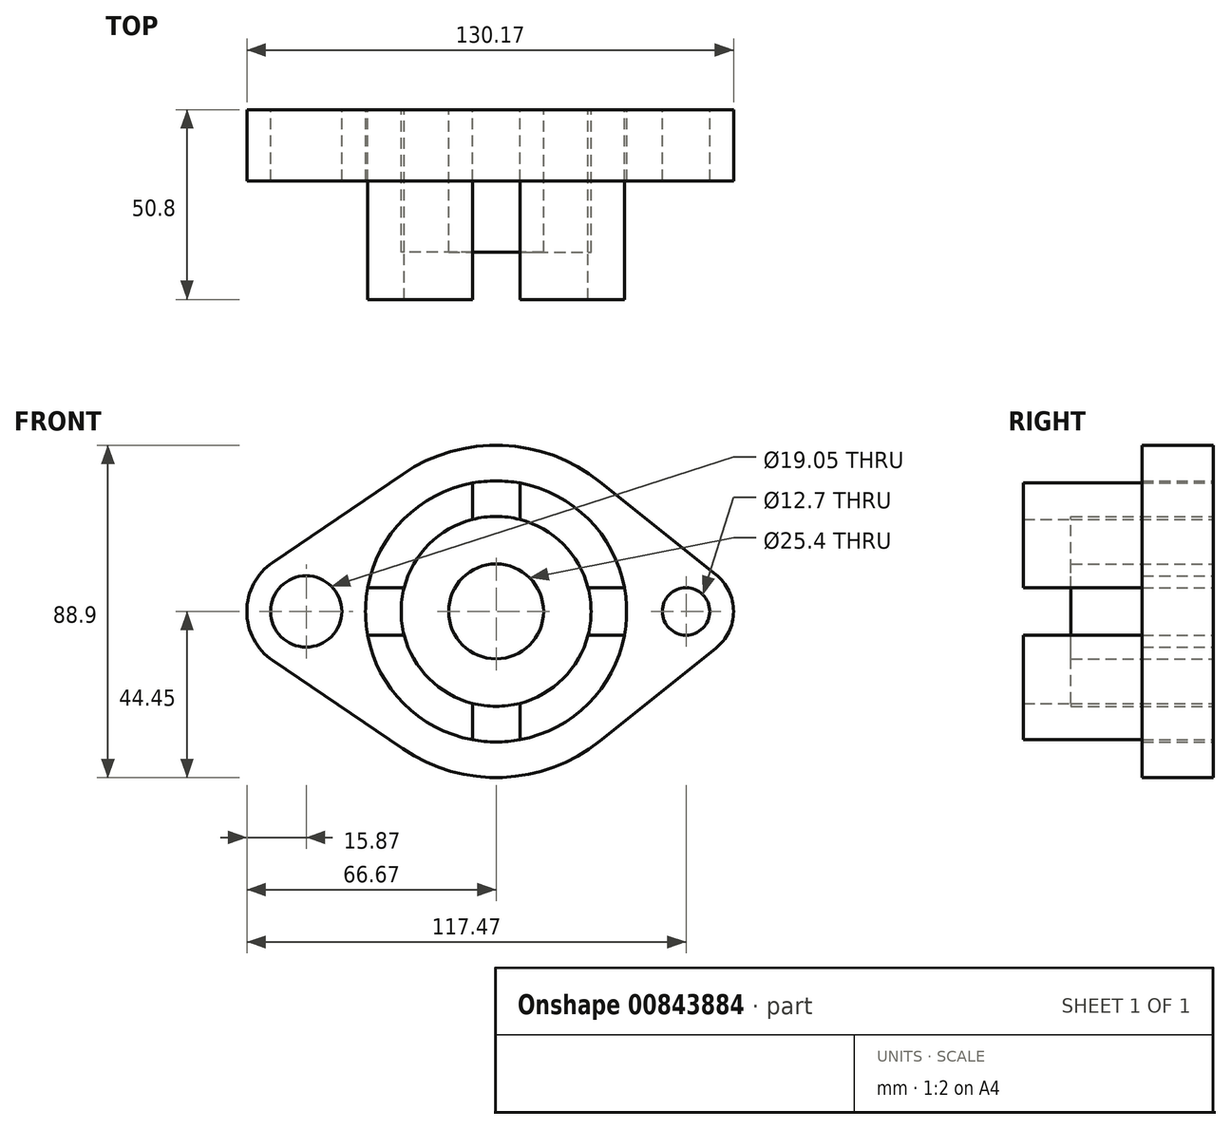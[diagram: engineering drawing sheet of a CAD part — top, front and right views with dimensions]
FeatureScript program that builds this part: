
annotation { "Feature Type Name" : "Feature", "Feature Type Description" : "" }
export const myFeature = defineFeature(function(context is Context, id is Id, definition is map)
    precondition{}
    {
        {
            var Q0;
            Q0=qCreatedBy(makeId("Front.planeOp"),FACE);
            var sketch = newSketch(context, id + "F0", { "sketchPlane" : qUnion([Q0])});
            skCircle(sketch, "E0", {"center": v(0, 0) * mm, "radius": 12.7 * mm});
            skCircle(sketch, "E1", {"center": v(0, 0) * mm, "radius": 25.4 * mm});
            skCircle(sketch, "E2", {"center": v(0, 0) * mm, "radius": 34.93 * mm});
            skLineSegment(sketch, "E3", {"start": v(24.6, 6.35) * mm, "end": v(34.34, 6.35) * mm});
            skLineSegment(sketch, "E4", {"start": v(24.6, -6.35) * mm, "end": v(34.34, -6.35) * mm});
            skLineSegment(sketch, "E5", {"start": v(6.35, 24.6) * mm, "end": v(6.35, 34.34) * mm});
            skLineSegment(sketch, "E6", {"start": v(-6.35, 24.6) * mm, "end": v(-6.35, 34.34) * mm});
            skLineSegment(sketch, "E7", {"start": v(-24.6, 6.35) * mm, "end": v(-34.34, 6.35) * mm});
            skLineSegment(sketch, "E8", {"start": v(-24.6, -6.35) * mm, "end": v(-34.34, -6.35) * mm});
            skLineSegment(sketch, "E9", {"start": v(6.35, -24.6) * mm, "end": v(6.35, -34.34) * mm});
            skLineSegment(sketch, "E10", {"start": v(-6.35, -24.6) * mm, "end": v(-6.35, -34.34) * mm});
            skLineSegment(sketch, "E11", {"start": v(0, 0) * mm, "end": v(50.8, 0) * mm});
            skLineSegment(sketch, "E12", {"start": v(0, 0) * mm, "end": v(-50.8, 0) * mm});
            skCircle(sketch, "E13", {"center": v(50.8, 0) * mm, "radius": 6.35 * mm});
            skCircle(sketch, "E14", {"center": v(-50.8, 0) * mm, "radius": 9.53 * mm});
            skArc(sketch, "E15", {"start": v(-25, -36.75) * mm, "mid": v(1.73, -44.42) * mm, "end": v(27.78, -34.7) * mm});
            skArc(sketch, "E16", {"start": v(58.74, -9.91) * mm, "mid": v(63.5, 0) * mm, "end": v(58.74, 9.91) * mm});
            skArc(sketch, "E17", {"start": v(-59.73, 13.13) * mm, "mid": v(-66.68, 0) * mm, "end": v(-59.73, -13.13) * mm});
            skLineSegment(sketch, "E18", {"start": v(58.74, 9.91) * mm, "end": v(27.78, 34.7) * mm});
            skLineSegment(sketch, "E19", {"start": v(27.78, -34.7) * mm, "end": v(58.74, -9.91) * mm});
            skLineSegment(sketch, "E20", {"start": v(-59.73, -13.13) * mm, "end": v(-25, -36.75) * mm});
            skLineSegment(sketch, "E21", {"start": v(-59.73, 13.13) * mm, "end": v(-25, 36.75) * mm});
            skArc(sketch, "E22.trimOffspring", {"start": v(27.78, 34.7) * mm, "mid": v(1.73, 44.42) * mm, "end": v(-25, 36.75) * mm});
            skSolve(sketch);
        }
        {
            var Q0;
            Q0=makeQuery(id+"F0.imprint","IMPRINT",FACE,{"disambiguationData":[TD([[makeQuery(id+"F0.imprint","IMPRINT",EDGE,{"derivedFrom":sQuery(id+"F0.wireOp",EDGE,"E13")}),-1.0]])]});
            extrude(context, id + "F1", {"entities" : qUnion([Q0]), "depth" : 19.05 * mm, "offsetDistance" : 25.4 * mm});
        }
        {
            var Q0;
            {var subQ0=sQuery(id+"F0.wireOp",EDGE,"E6");Q0=makeQuery(id+"F0.imprint","IMPRINT",FACE,{"disambiguationData":[TD([[makeQuery(id+"F0.imprint","IMPRINT",EDGE,{"derivedFrom":subQ0}),1.0]])]});}
            var Q1;
            {var subQ0=sQuery(id+"F0.wireOp",EDGE,"E3");Q1=makeQuery(id+"F0.imprint","IMPRINT",FACE,{"disambiguationData":[TD([[makeQuery(id+"F0.imprint","IMPRINT",EDGE,{"derivedFrom":subQ0}),1.0]])]});}
            var Q2;
            {var subQ0=sQuery(id+"F0.wireOp",EDGE,"E4");Q2=makeQuery(id+"F0.imprint","IMPRINT",FACE,{"disambiguationData":[TD([[makeQuery(id+"F0.imprint","IMPRINT",EDGE,{"derivedFrom":subQ0}),-1.0]])]});}
            var Q3;
            {var subQ0=sQuery(id+"F0.wireOp",EDGE,"E8");Q3=makeQuery(id+"F0.imprint","IMPRINT",FACE,{"disambiguationData":[TD([[makeQuery(id+"F0.imprint","IMPRINT",EDGE,{"derivedFrom":subQ0}),1.0]])]});}
            extrude(context, id + "F2", {"entities" : qUnion([Q0, Q1, Q2, Q3]), "operationType" : NewBodyOperationType.ADD, "depth" : 50.8 * mm, "offsetDistance" : 25.4 * mm});
        }
        {
            var Q0;
            {var subQ3=sQuery(id+"F0.wireOp",EDGE,"E11");var subQ4=sQuery(id+"F0.wireOp",EDGE,"E0");var subQ5=makeQuery(id+"F0.imprint","INTERSECT",VERTEX,{"derivedFrom":[subQ4,subQ3]});Q0=makeQuery(id+"F0.imprint","IMPRINT",FACE,{"disambiguationData":[TD([[makeQuery(id+"F0.imprint","IMPRINT",EDGE,{"disambiguationData":[TD([[subQ5,1.0]])],"derivedFrom":subQ4}),-1.0]])]});}
            var Q1;
            {var subQ4=sQuery(id+"F0.wireOp",EDGE,"E11");var subQ6=sQuery(id+"F0.wireOp",EDGE,"E0");var subQ7=makeQuery(id+"F0.imprint","INTERSECT",VERTEX,{"derivedFrom":[subQ6,subQ4]});Q1=makeQuery(id+"F0.imprint","IMPRINT",FACE,{"disambiguationData":[TD([[makeQuery(id+"F0.imprint","IMPRINT",EDGE,{"disambiguationData":[TD([[subQ7,-1.0]])],"derivedFrom":subQ6}),-1.0]])]});}
            extrude(context, id + "F3", {"entities" : qUnion([Q0, Q1]), "operationType" : NewBodyOperationType.ADD, "depth" : 38.1 * mm, "offsetDistance" : 25.4 * mm});
        }
    });
